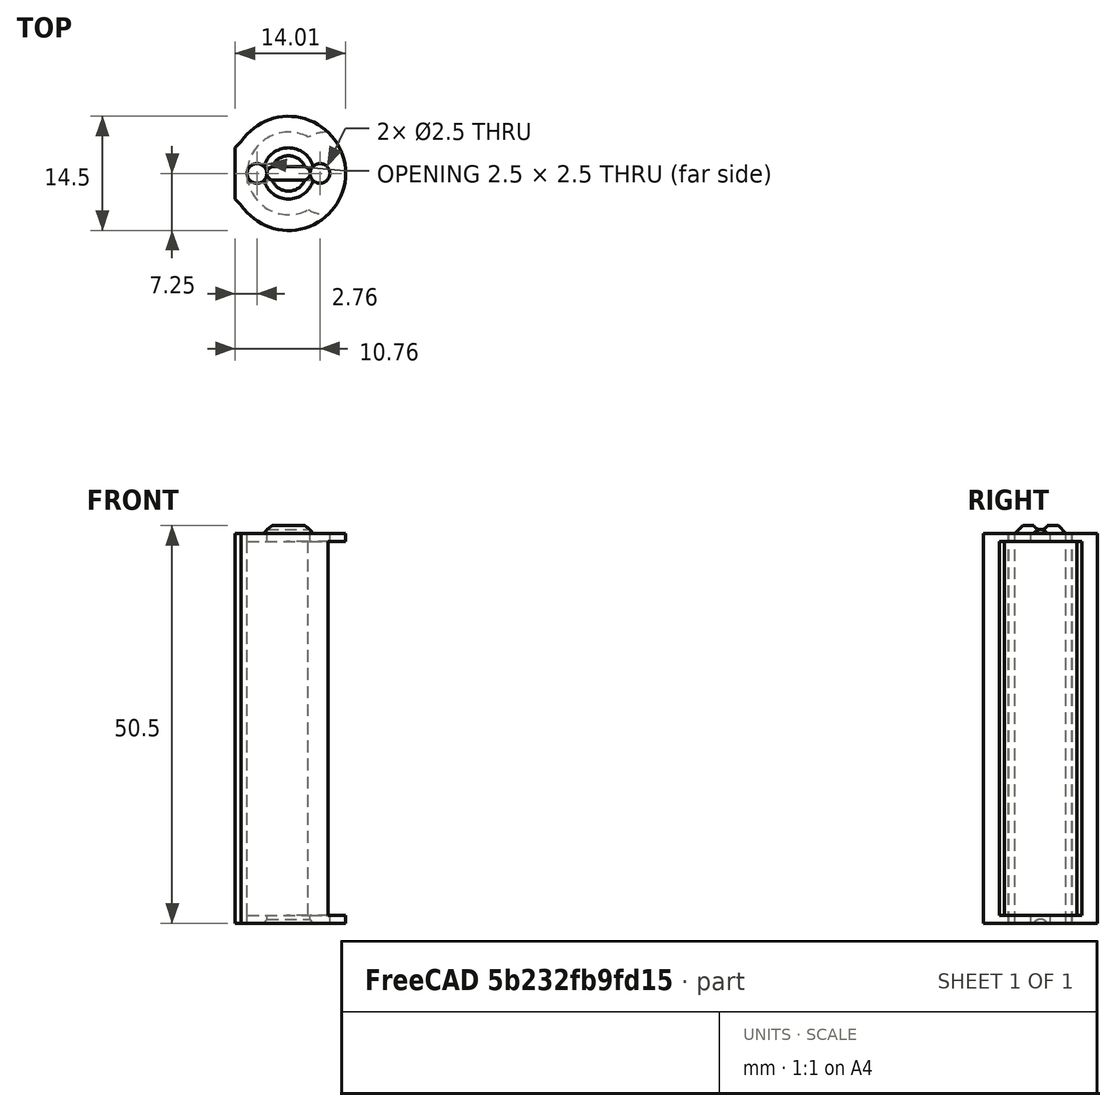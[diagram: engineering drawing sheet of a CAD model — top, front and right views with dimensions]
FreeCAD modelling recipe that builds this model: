
FCSTD DOCUMENT  (FreeCAD 0.18.4R)
Label: aabattery
License: All rights reserved
LicenseURL: http://en.wikipedia.org/wiki/All_rights_reserved
objects: Part::Cylinder×8, Part::MultiFuse×4, Part::Cut×3, Part::Chamfer×2, Part::Box×2
note: 19 computed .brp shape members not serialized (recipe doc carries the construction recipe); baked Part::Feature solids carry a one-line shape summary decoded from their .brp

FEATURE [Part::Cylinder] Cylinder
  Angle = 360
  AttacherType = Attacher::AttachEngine3D
  Height = 49.5
  Radius = 7.25
FEATURE [Part::Cylinder] Cylinder001
  Angle = 360
  AttacherType = Attacher::AttachEngine3D
  Height = 50.5
  Radius = 3.25
FEATURE [Part::Cylinder] Cylinder002
  Angle = 360
  AttacherType = Attacher::AttachEngine3D
  Height = 47.5
  Placement = pos=(0,0,1) rot=(0,0,1;0rad)
  Radius = 5.25
FEATURE [Part::Cylinder] Cylinder003
  Angle = 360
  AttacherType = Attacher::AttachEngine3D
  Height = 47.5
  Placement = pos=(5,0,1) rot=(0,0,1;0rad)
  Radius = 5.25
FEATURE [Part::MultiFuse] Fusion001
  Shapes = -> [Cylinder003,Cylinder002]
FEATURE [Part::Cylinder] Cylinder004
  Angle = 360
  AttacherType = Attacher::AttachEngine3D
  Height = 55
  Placement = pos=(4,0,0) rot=(0,0,1;0rad)
  Radius = 1.25
FEATURE [Part::Cylinder] Cylinder005
  Angle = 360
  AttacherType = Attacher::AttachEngine3D
  Height = 55
  Placement = pos=(-4,0,0) rot=(0,0,1;0rad)
  Radius = 1.25
FEATURE [Part::Cylinder] Cylinder006
  Angle = 360
  AttacherType = Attacher::AttachEngine3D
  Height = 8
  Placement = pos=(-4,0,51) rot=(0,1,0;1.5708rad)
  Radius = 1
FEATURE [Part::Cylinder] Cylinder007
  Angle = 360
  AttacherType = Attacher::AttachEngine3D
  Height = 8
  Placement = pos=(-4,0,-0.5) rot=(0,1,0;1.5708rad)
  Radius = 1
FEATURE [Part::MultiFuse] Fusion002
  Shapes = -> [Cylinder006,Cylinder005,Cylinder004,Cylinder007]
FEATURE [Part::Chamfer] Chamfer
  Base = -> Cylinder001
  Edges = 2 edges r=1: [Edge1,Edge3]
FEATURE [Part::MultiFuse] Fusion
  Shapes = -> [Cylinder,Chamfer]
FEATURE [Part::Cut] Cut
  Base = -> Fusion
  Tool = -> Fusion001
FEATURE [Part::Cut] Cut001
  Base = -> Cut
  Tool = -> Fusion002
FEATURE [Part::Box] Box  label="Cube"
  AttacherType = Attacher::AttachEngine3D
  Height = 60
  Length = 5
  Placement = pos=(-11,-10,-4) rot=(0,0,1;0rad)
  Width = 20
FEATURE [Part::Cut] Cut002
  Base = -> Cut001
  Tool = -> Box
FEATURE [Part::Box] Box001  label="Cube001"
  AttacherType = Attacher::AttachEngine3D
  Height = 49.5
  Length = 1.51
  Placement = pos=(-6.76,-4.75,0) rot=(0,0,1;0rad)
  Width = 9.5
FEATURE [Part::Chamfer] Chamfer001
  Base = -> Box001
  Edges = 2 edges r=1.5: [Edge1,Edge3]
FEATURE [Part::MultiFuse] Fusion003
  Shapes = -> [Cut002,Chamfer001]
